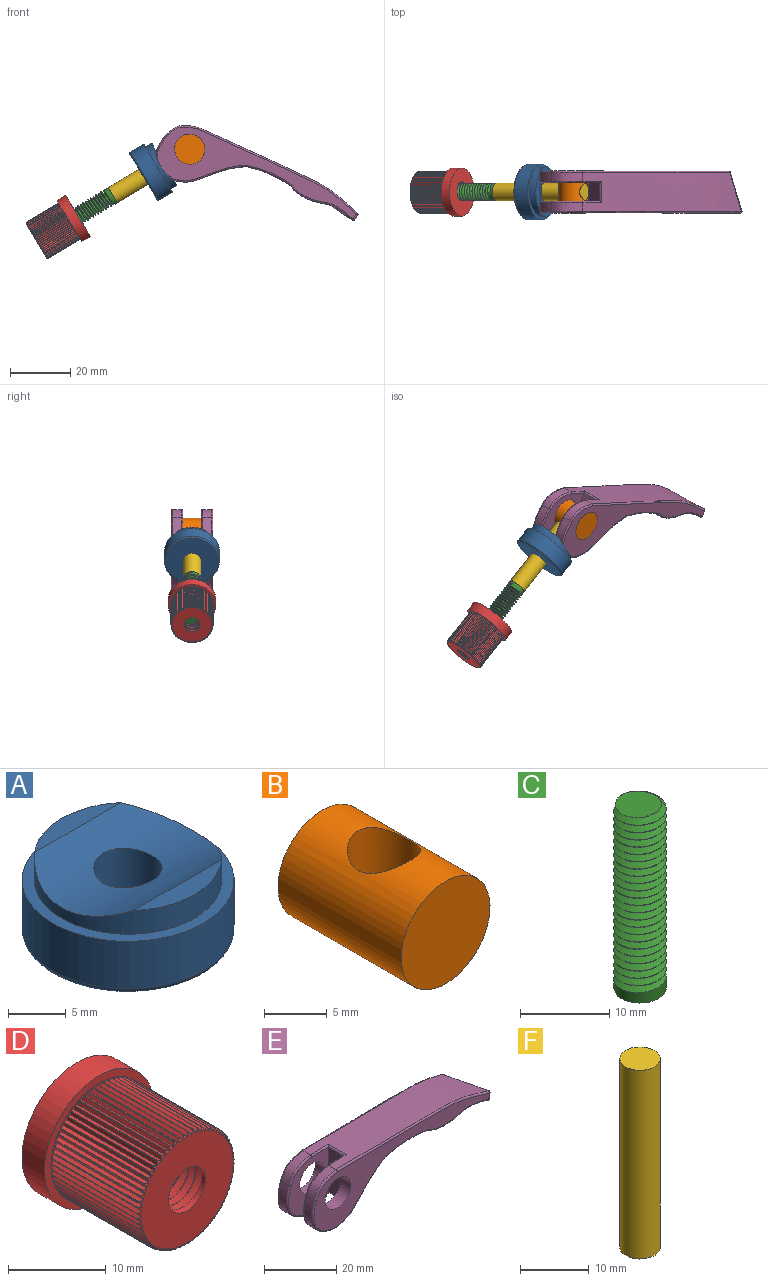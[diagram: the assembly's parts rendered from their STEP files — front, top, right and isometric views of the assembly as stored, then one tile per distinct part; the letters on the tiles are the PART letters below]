
ASSEMBLY  parts=6 mates=5
PART A: 9 faces, bbox 19.9x19.9x8.1 mm
  f0: plane 10.78x2.05mm, normal (0,0,1), area 15.1mm2, adj f5,f8
  f1: cylinder r=9.2mm len=18.4mm, axis (0,0,-1), area 291.9mm2, adj f2,f7
  f2: plane 18.4x18.4mm, normal (0,0,1), area 58.5mm2, adj f1,f5
  f3: plane 17.4x17.4mm, normal (0,0,-1), area 210.3mm2, adj f4,f7
  f4: cylinder r=2.96mm len=7mm, axis (0,0,-1), area 127mm2, adj f3,f8
  f5: cylinder r=8.12mm len=16.25mm, axis (0,0,-1), area 103.6mm2, adj f0,f2,f6,f8
  f6: plane 10.55x1.94mm, normal (0,0,1), area 14mm2, adj f5,f8
  f7: torus R=8.7mm, axis (0,0,1), area 44.5mm2, adj f1,f3
  f8: cylinder r=14.26mm len=16.25mm, axis (1,0,0), area 155.9mm2, adj f0,f4,f5,f6
PART B: 4 faces, bbox 10x13.9x10 mm
  f0: cylinder r=5mm len=13.9mm, axis (0,1,0), area 380.3mm2, adj f1,f2,f3
  f1: plane 10x10mm, normal (0,-1,0), area 78.5mm2, adj f0
  f2: plane 10x10mm, normal (0,1,0), area 78.5mm2, adj f0
  f3: cylinder r=2.93mm len=10mm, axis (0,0,-1), area 166.9mm2, adj f0
PART C: 30 faces, bbox 6.5x7.4x26.2 mm
  f0: cylinder r=2.95mm len=5.9mm, axis (0,0,-1), area 24.5mm2, adj f24,f26,f27,f28,f29
  f1: cylinder r=2.95mm len=0.13mm, axis (0,0,-1), area 0mm2, adj f2,f25,f28
  f2: cylinder r=2.95mm len=5.9mm, axis (0,0,-1), area 1.1mm2, adj f1,f3,f25,f27,f28
  f3: cylinder r=2.95mm len=5.9mm, axis (0,0,-1), area 1.2mm2, adj f2,f4,f27,f28
  f4: cylinder r=2.95mm len=5.9mm, axis (0,0,-1), area 1.2mm2, adj f3,f5,f27,f28
  f5: cylinder r=2.95mm len=5.9mm, axis (0,0,-1), area 1.2mm2, adj f4,f6,f27,f28
  f6: cylinder r=2.95mm len=5.9mm, axis (0,0,-1), area 1.2mm2, adj f5,f7,f27,f28
  f7: cylinder r=2.95mm len=5.9mm, axis (0,0,-1), area 1.2mm2, adj f6,f8,f27,f28
  f8: cylinder r=2.95mm len=5.9mm, axis (0,0,-1), area 1.2mm2, adj f7,f9,f27,f28
  f9: cylinder r=2.95mm len=5.9mm, axis (0,0,-1), area 1.2mm2, adj f8,f10,f27,f28
  f10: cylinder r=2.95mm len=5.9mm, axis (0,0,-1), area 1.2mm2, adj f9,f11,f27,f28
  f11: cylinder r=2.95mm len=5.9mm, axis (0,0,-1), area 1.2mm2, adj f10,f12,f27,f28
  f12: cylinder r=2.95mm len=5.9mm, axis (0,0,-1), area 1.2mm2, adj f11,f13,f27,f28
  f13: cylinder r=2.95mm len=5.9mm, axis (0,0,-1), area 1.2mm2, adj f12,f14,f27,f28
  f14: cylinder r=2.95mm len=5.9mm, axis (0,0,-1), area 1.2mm2, adj f13,f15,f27,f28
  f15: cylinder r=2.95mm len=5.9mm, axis (0,0,-1), area 1.2mm2, adj f14,f16,f27,f28
  f16: cylinder r=2.95mm len=5.9mm, axis (0,0,-1), area 1.2mm2, adj f15,f17,f27,f28
  f17: cylinder r=2.95mm len=5.9mm, axis (0,0,-1), area 1.2mm2, adj f16,f18,f27,f28
  f18: cylinder r=2.95mm len=5.9mm, axis (0,0,-1), area 1.2mm2, adj f17,f19,f27,f28
  f19: cylinder r=2.95mm len=5.9mm, axis (0,0,-1), area 1.2mm2, adj f18,f20,f27,f28
  f20: cylinder r=2.95mm len=5.9mm, axis (0,0,-1), area 1.2mm2, adj f19,f21,f27,f28
  f21: cylinder r=2.95mm len=5.9mm, axis (0,0,-1), area 1.2mm2, adj f20,f22,f27,f28
  f22: cylinder r=2.95mm len=5.9mm, axis (0,0,-1), area 1.2mm2, adj f21,f23,f27,f28
  f23: cylinder r=2.95mm len=5.9mm, axis (0,0,-1), area 1.2mm2, adj f22,f24,f27,f28
  f24: cylinder r=2.95mm len=5.9mm, axis (0,0,-1), area 1.2mm2, adj f0,f23,f27,f28
  f25: plane 5.73x5.71mm, normal (0,0,1), area 20.9mm2, adj f1,f2,f27,f28
  f26: plane 5.9x5.9mm, normal (0,0,-1), area 27.3mm2, adj f0
  f27: bspline ~24.81x6.84mm, area 362.6mm2, adj f0,f2,f3,f4,f5,f6,f7,f8
  f28: bspline ~24.31x6.84mm, area 352.4mm2, adj f0,f1,f2,f3,f4,f5,f6,f7
  f29: plane 0.94x0.81mm, normal (0,1,0), area 0.4mm2, adj f0,f27,f28
PART D: 280 faces, bbox 16.4x17.2x16.4 mm
  f0: cylinder r=7mm len=14mm, axis (0,1,0), area 36.4mm2, adj f2,f3,f4,f5,f6,f7,f8,f9
  f1: plane 13.34x13.34mm, normal (0,-1,0), area 117.5mm2, adj f2,f3,f4,f5,f6,f7,f8,f9
  f2: torus R=6.67mm, axis (0,-1,0), area 0.1mm2, adj f0,f1,f88,f278
  f3: torus R=6.67mm, axis (0,-1,0), area 0.1mm2, adj f0,f1,f275,f279
  f4: torus R=6.67mm, axis (0,-1,0), area 0.1mm2, adj f0,f1,f272,f274
  f5: torus R=6.67mm, axis (0,-1,0), area 0.1mm2, adj f0,f1,f269,f271
  f6: torus R=6.67mm, axis (0,-1,0), area 0.1mm2, adj f0,f1,f266,f268
  f7: torus R=6.67mm, axis (0,-1,0), area 0.1mm2, adj f0,f1,f263,f265
  f8: torus R=6.67mm, axis (0,-1,0), area 0.1mm2, adj f0,f1,f260,f262
  f9: torus R=6.67mm, axis (0,-1,0), area 0.1mm2, adj f0,f1,f257,f259
  f10: torus R=6.67mm, axis (0,-1,0), area 0.1mm2, adj f0,f1,f254,f256
  f11: torus R=6.67mm, axis (0,-1,0), area 0.1mm2, adj f0,f1,f251,f253
  f12: torus R=6.67mm, axis (0,-1,0), area 0.1mm2, adj f0,f1,f248,f250
  f13: torus R=6.67mm, axis (0,-1,0), area 0.1mm2, adj f0,f1,f245,f247
  f14: torus R=6.67mm, axis (0,-1,0), area 0.1mm2, adj f0,f1,f242,f244
  f15: torus R=6.67mm, axis (0,-1,0), area 0.1mm2, adj f0,f1,f239,f241
  f16: torus R=6.67mm, axis (0,-1,0), area 0.1mm2, adj f0,f1,f236,f238
  f17: torus R=6.67mm, axis (0,-1,0), area 0.1mm2, adj f0,f1,f233,f235
  f18: torus R=6.67mm, axis (0,-1,0), area 0.1mm2, adj f0,f1,f230,f232
  f19: torus R=6.67mm, axis (0,-1,0), area 0.1mm2, adj f0,f1,f227,f229
  f20: torus R=6.67mm, axis (0,-1,0), area 0.1mm2, adj f0,f1,f224,f226
  f21: torus R=6.67mm, axis (0,-1,0), area 0.1mm2, adj f0,f1,f221,f223
  f22: torus R=6.67mm, axis (0,-1,0), area 0.1mm2, adj f0,f1,f218,f220
  f23: torus R=6.67mm, axis (0,-1,0), area 0.1mm2, adj f0,f1,f215,f217
  f24: torus R=6.67mm, axis (0,-1,0), area 0.1mm2, adj f0,f1,f212,f214
  f25: torus R=6.67mm, axis (0,-1,0), area 0.1mm2, adj f0,f1,f209,f211
  f26: torus R=6.67mm, axis (0,-1,0), area 0.1mm2, adj f0,f1,f206,f208
  f27: torus R=6.67mm, axis (0,-1,0), area 0.1mm2, adj f0,f1,f203,f205
  f28: torus R=6.67mm, axis (0,-1,0), area 0.1mm2, adj f0,f1,f200,f202
  f29: torus R=6.67mm, axis (0,-1,0), area 0.1mm2, adj f0,f1,f197,f199
  f30: torus R=6.67mm, axis (0,-1,0), area 0.1mm2, adj f0,f1,f194,f196
  f31: torus R=6.67mm, axis (0,-1,0), area 0.1mm2, adj f0,f1,f191,f193
  f32: torus R=6.67mm, axis (0,-1,0), area 0.1mm2, adj f0,f1,f188,f190
  f33: torus R=6.67mm, axis (0,-1,0), area 0.1mm2, adj f0,f1,f185,f187
  f34: torus R=6.67mm, axis (0,-1,0), area 0.1mm2, adj f0,f1,f182,f184
  f35: torus R=6.67mm, axis (0,-1,0), area 0.1mm2, adj f0,f1,f179,f181
  f36: torus R=6.67mm, axis (0,-1,0), area 0.1mm2, adj f0,f1,f176,f178
  f37: torus R=6.67mm, axis (0,-1,0), area 0.1mm2, adj f0,f1,f173,f175
  f38: torus R=6.67mm, axis (0,-1,0), area 0.1mm2, adj f0,f1,f170,f172
  f39: torus R=6.67mm, axis (0,-1,0), area 0.1mm2, adj f0,f1,f167,f169
  f40: torus R=6.67mm, axis (0,-1,0), area 0.1mm2, adj f0,f1,f164,f166
  f41: torus R=6.67mm, axis (0,-1,0), area 0.1mm2, adj f0,f1,f161,f163
  f42: torus R=6.67mm, axis (0,-1,0), area 0.1mm2, adj f0,f1,f158,f160
  f43: torus R=6.67mm, axis (0,-1,0), area 0.1mm2, adj f0,f1,f155,f157
  f44: torus R=6.67mm, axis (0,-1,0), area 0.1mm2, adj f0,f1,f152,f154
  f45: torus R=6.67mm, axis (0,-1,0), area 0.1mm2, adj f0,f1,f149,f151
  f46: torus R=6.67mm, axis (0,-1,0), area 0.1mm2, adj f0,f1,f146,f148
  f47: torus R=6.67mm, axis (0,-1,0), area 0.1mm2, adj f0,f1,f143,f145
  f48: torus R=6.67mm, axis (0,-1,0), area 0.1mm2, adj f0,f1,f140,f142
  f49: torus R=6.67mm, axis (0,-1,0), area 0.1mm2, adj f0,f1,f137,f139
  f50: torus R=6.67mm, axis (0,-1,0), area 0.1mm2, adj f0,f1,f134,f136
  f51: torus R=6.67mm, axis (0,-1,0), area 0.1mm2, adj f0,f1,f131,f133
  f52: torus R=6.67mm, axis (0,-1,0), area 0.1mm2, adj f0,f1,f128,f130
  f53: torus R=6.67mm, axis (0,-1,0), area 0.1mm2, adj f0,f1,f125,f127
  f54: torus R=6.67mm, axis (0,-1,0), area 0.1mm2, adj f0,f1,f122,f124
  f55: torus R=6.67mm, axis (0,-1,0), area 0.1mm2, adj f0,f1,f119,f121
  f56: torus R=6.67mm, axis (0,-1,0), area 0.1mm2, adj f0,f1,f116,f118
  f57: torus R=6.67mm, axis (0,-1,0), area 0.1mm2, adj f0,f1,f113,f115
  f58: torus R=6.67mm, axis (0,-1,0), area 0.1mm2, adj f0,f1,f110,f112
  f59: torus R=6.67mm, axis (0,-1,0), area 0.1mm2, adj f0,f1,f107,f109
  f60: torus R=6.67mm, axis (0,-1,0), area 0.1mm2, adj f0,f1,f104,f106
  f61: torus R=6.67mm, axis (0,-1,0), area 0.1mm2, adj f0,f1,f101,f103
  f62: torus R=6.67mm, axis (0,-1,0), area 0.1mm2, adj f0,f1,f98,f100
  f63: torus R=6.67mm, axis (0,-1,0), area 0.1mm2, adj f0,f1,f95,f97
  f64: torus R=6.67mm, axis (0,-1,0), area 0.1mm2, adj f0,f1,f92,f94
  f65: torus R=6.67mm, axis (0,-1,0), area 0.1mm2, adj f0,f1,f89,f91
  f66: cylinder r=7.95mm len=15.9mm, axis (0,1,0), area 162.3mm2, adj f67,f68
  f67: plane 15.9x15.9mm, normal (0,-1,0), area 44.6mm2, adj f0,f66
  f68: plane 16.45x16.45mm, normal (0,1,0), area 169.7mm2, adj f66,f84,f85,f86
  f69: cylinder r=2.67mm len=5.33mm, axis (0,1,0), area 8.9mm2, adj f1,f70,f85,f86,f87
  f70: cylinder r=2.67mm len=5.33mm, axis (0,1,0), area 1.6mm2, adj f69,f71,f85,f86
  f71: cylinder r=2.67mm len=5.33mm, axis (0,1,0), area 1.6mm2, adj f70,f72,f85,f86
  f72: cylinder r=2.67mm len=5.33mm, axis (0,1,0), area 1.6mm2, adj f71,f73,f85,f86
  f73: cylinder r=2.67mm len=5.33mm, axis (0,1,0), area 1.6mm2, adj f72,f74,f85,f86
  f74: cylinder r=2.67mm len=5.33mm, axis (0,1,0), area 1.6mm2, adj f73,f75,f85,f86
  f75: cylinder r=2.67mm len=5.33mm, axis (0,1,0), area 1.6mm2, adj f74,f76,f85,f86
  f76: cylinder r=2.67mm len=5.33mm, axis (0,1,0), area 1.6mm2, adj f75,f77,f85,f86
  f77: cylinder r=2.67mm len=5.33mm, axis (0,1,0), area 1.6mm2, adj f76,f78,f85,f86
  f78: cylinder r=2.67mm len=5.33mm, axis (0,1,0), area 1.6mm2, adj f77,f79,f85,f86
  f79: cylinder r=2.67mm len=5.33mm, axis (0,1,0), area 1.6mm2, adj f78,f80,f85,f86
  f80: cylinder r=2.67mm len=5.33mm, axis (0,1,0), area 1.6mm2, adj f79,f81,f85,f86
  f81: cylinder r=2.67mm len=5.33mm, axis (0,1,0), area 1.6mm2, adj f80,f82,f85,f86
  f82: cylinder r=2.67mm len=5.33mm, axis (0,1,0), area 1.6mm2, adj f81,f83,f85,f86
  f83: cylinder r=2.67mm len=5.33mm, axis (0,1,0), area 1.6mm2, adj f82,f84,f85,f86
  f84: cylinder r=2.67mm len=5.33mm, axis (0,1,0), area 1.5mm2, adj f68,f83,f85,f86
  f85: bspline ~16.47x7.96mm, area 271.9mm2, adj f68,f69,f70,f71,f72,f73,f74,f75
  f86: bspline ~16.15x7.96mm, area 267.8mm2, adj f68,f69,f70,f71,f72,f73,f74,f75
  f87: plane 0.9x0.78mm, normal (0,0,1), area 0.4mm2, adj f69,f85,f86
  f88: plane 12.7x0.36mm, normal (-0.78,0,0.63), area 5.8mm2, adj f0,f1,f2,f89,f90
  f89: plane 12.7x0.35mm, normal (0.64,0,0.77), area 5.8mm2, adj f0,f1,f65,f88,f90
  f90: plane 0.64x0.36mm, normal (0,-1,0), area 0.1mm2, adj f0,f88,f89
  f91: plane 12.7x0.38mm, normal (-0.84,0,0.55), area 5.8mm2, adj f0,f1,f65,f92,f93
  f92: plane 12.7x0.38mm, normal (0.56,0,0.83), area 5.8mm2, adj f0,f1,f64,f91,f93
  f93: plane 0.63x0.38mm, normal (0,-1,0), area 0.1mm2, adj f0,f91,f92
  f94: plane 12.7x0.41mm, normal (-0.89,0,0.46), area 5.8mm2, adj f0,f1,f64,f95,f96
  f95: plane 12.7x0.4mm, normal (0.48,0,0.88), area 5.8mm2, adj f0,f1,f63,f94,f96
  f96: plane 0.62x0.41mm, normal (0,-1,0), area 0.1mm2, adj f0,f94,f95
  f97: plane 12.7x0.43mm, normal (-0.93,0,0.38), area 5.8mm2, adj f0,f1,f63,f98,f99
  f98: plane 12.7x0.42mm, normal (0.39,0,0.92), area 5.8mm2, adj f0,f1,f62,f97,f99
  f99: plane 0.59x0.43mm, normal (0,-1,0), area 0.1mm2, adj f0,f97,f98
  f100: plane 12.7x0.44mm, normal (-0.96,0,0.28), area 5.8mm2, adj f0,f1,f62,f101,f102
  f101: plane 12.7x0.44mm, normal (0.3,0,0.95), area 5.8mm2, adj f0,f1,f61,f100,f102
  f102: plane 0.57x0.44mm, normal (0,-1,0), area 0.1mm2, adj f0,f100,f101
  f103: plane 12.7x0.45mm, normal (-0.98,0,0.19), area 5.8mm2, adj f0,f1,f61,f104,f105
  f104: plane 12.7x0.45mm, normal (0.2,0,0.98), area 5.8mm2, adj f0,f1,f60,f103,f105
  f105: plane 0.54x0.45mm, normal (0,-1,0), area 0.1mm2, adj f0,f103,f104
  f106: plane 12.7x0.46mm, normal (-1,0,0.09), area 5.8mm2, adj f0,f1,f60,f107,f108
  f107: plane 12.7x0.46mm, normal (0.11,0,0.99), area 5.8mm2, adj f0,f1,f59,f106,f108
  f108: plane 0.5x0.46mm, normal (0,-1,0), area 0.1mm2, adj f0,f106,f107
  f109: plane 12.7x0.46mm, normal (-1,0,-0.01), area 5.8mm2, adj f0,f1,f59,f110,f111
  f110: plane 12.7x0.46mm, normal (0.01,0,1), area 5.8mm2, adj f0,f1,f58,f109,f111
  f111: plane 0.46x0.46mm, normal (0,-1,0), area 0.1mm2, adj f0,f109,f110
  f112: plane 12.7x0.46mm, normal (-0.99,0,-0.11), area 5.8mm2, adj f0,f1,f58,f113,f114
  f113: plane 12.7x0.46mm, normal (-0.09,0,1), area 5.8mm2, adj f0,f1,f57,f112,f114
  f114: plane 0.5x0.46mm, normal (0,-1,0), area 0.1mm2, adj f0,f112,f113
  f115: plane 12.7x0.45mm, normal (-0.98,0,-0.2), area 5.8mm2, adj f0,f1,f57,f116,f117
  f116: plane 12.7x0.45mm, normal (-0.19,0,0.98), area 5.8mm2, adj f0,f1,f56,f115,f117
  f117: plane 0.54x0.45mm, normal (0,-1,0), area 0.1mm2, adj f0,f115,f116
  f118: plane 12.7x0.44mm, normal (-0.95,0,-0.3), area 5.8mm2, adj f0,f1,f56,f119,f120
  f119: plane 12.7x0.44mm, normal (-0.28,0,0.96), area 5.8mm2, adj f0,f1,f55,f118,f120
  f120: plane 0.57x0.44mm, normal (0,-1,0), area 0.1mm2, adj f0,f118,f119
  f121: plane 12.7x0.42mm, normal (-0.92,0,-0.39), area 5.8mm2, adj f0,f1,f55,f122,f123
  f122: plane 12.7x0.43mm, normal (-0.38,0,0.93), area 5.8mm2, adj f0,f1,f54,f121,f123
  f123: plane 0.59x0.43mm, normal (0,-1,0), area 0.1mm2, adj f0,f121,f122
  f124: plane 12.7x0.4mm, normal (-0.88,0,-0.48), area 5.8mm2, adj f0,f1,f54,f125,f126
  f125: plane 12.7x0.41mm, normal (-0.46,0,0.89), area 5.8mm2, adj f0,f1,f53,f124,f126
  f126: plane 0.62x0.41mm, normal (0,-1,0), area 0.1mm2, adj f0,f124,f125
  f127: plane 12.7x0.38mm, normal (-0.83,0,-0.56), area 5.8mm2, adj f0,f1,f53,f128,f129
  f128: plane 12.7x0.38mm, normal (-0.55,0,0.84), area 5.8mm2, adj f0,f1,f52,f127,f129
  f129: plane 0.63x0.38mm, normal (0,-1,0), area 0.1mm2, adj f0,f127,f128
  f130: plane 12.7x0.35mm, normal (-0.77,0,-0.64), area 5.8mm2, adj f0,f1,f52,f131,f132
  f131: plane 12.7x0.36mm, normal (-0.63,0,0.78), area 5.8mm2, adj f0,f1,f51,f130,f132
  f132: plane 0.64x0.36mm, normal (0,-1,0), area 0.1mm2, adj f0,f130,f131
  f133: plane 12.7x0.33mm, normal (-0.7,0,-0.71), area 5.8mm2, adj f0,f1,f51,f134,f135
  f134: plane 12.7x0.33mm, normal (-0.7,0,0.71), area 5.8mm2, adj f0,f1,f50,f133,f135
  f135: plane 0.64x0.33mm, normal (0,-1,0), area 0.1mm2, adj f0,f133,f134
  f136: plane 12.7x0.36mm, normal (-0.63,0,-0.78), area 5.8mm2, adj f0,f1,f50,f137,f138
  f137: plane 12.7x0.35mm, normal (-0.77,0,0.64), area 5.8mm2, adj f0,f1,f49,f136,f138
  f138: plane 0.64x0.36mm, normal (0,-1,0), area 0.1mm2, adj f0,f136,f137
  f139: plane 12.7x0.38mm, normal (-0.55,0,-0.84), area 5.8mm2, adj f0,f1,f49,f140,f141
  f140: plane 12.7x0.38mm, normal (-0.83,0,0.56), area 5.8mm2, adj f0,f1,f48,f139,f141
  f141: plane 0.63x0.38mm, normal (0,-1,0), area 0.1mm2, adj f0,f139,f140
  f142: plane 12.7x0.41mm, normal (-0.46,0,-0.89), area 5.8mm2, adj f0,f1,f48,f143,f144
  f143: plane 12.7x0.4mm, normal (-0.88,0,0.48), area 5.8mm2, adj f0,f1,f47,f142,f144
  f144: plane 0.62x0.41mm, normal (0,-1,0), area 0.1mm2, adj f0,f142,f143
  f145: plane 12.7x0.43mm, normal (-0.38,0,-0.93), area 5.8mm2, adj f0,f1,f47,f146,f147
  f146: plane 12.7x0.42mm, normal (-0.92,0,0.39), area 5.8mm2, adj f0,f1,f46,f145,f147
  f147: plane 0.59x0.43mm, normal (0,-1,0), area 0.1mm2, adj f0,f145,f146
  f148: plane 12.7x0.44mm, normal (-0.28,0,-0.96), area 5.8mm2, adj f0,f1,f46,f149,f150
  f149: plane 12.7x0.44mm, normal (-0.95,0,0.3), area 5.8mm2, adj f0,f1,f45,f148,f150
  f150: plane 0.57x0.44mm, normal (0,-1,0), area 0.1mm2, adj f0,f148,f149
  f151: plane 12.7x0.45mm, normal (-0.19,0,-0.98), area 5.8mm2, adj f0,f1,f45,f152,f153
  f152: plane 12.7x0.45mm, normal (-0.98,0,0.2), area 5.8mm2, adj f0,f1,f44,f151,f153
  f153: plane 0.54x0.45mm, normal (0,-1,0), area 0.1mm2, adj f0,f151,f152
  f154: plane 12.7x0.46mm, normal (-0.09,0,-1), area 5.8mm2, adj f0,f1,f44,f155,f156
  f155: plane 12.7x0.46mm, normal (-0.99,0,0.11), area 5.8mm2, adj f0,f1,f43,f154,f156
  f156: plane 0.5x0.46mm, normal (0,-1,0), area 0.1mm2, adj f0,f154,f155
  f157: plane 12.7x0.46mm, normal (0.01,0,-1), area 5.8mm2, adj f0,f1,f43,f158,f159
  f158: plane 12.7x0.46mm, normal (-1,0,0.01), area 5.8mm2, adj f0,f1,f42,f157,f159
  f159: plane 0.46x0.46mm, normal (0,-1,0), area 0.1mm2, adj f0,f157,f158
  f160: plane 12.7x0.46mm, normal (0.11,0,-0.99), area 5.8mm2, adj f0,f1,f42,f161,f162
  f161: plane 12.7x0.46mm, normal (-1,0,-0.09), area 5.8mm2, adj f0,f1,f41,f160,f162
  f162: plane 0.5x0.46mm, normal (0,-1,0), area 0.1mm2, adj f0,f160,f161
  f163: plane 12.7x0.45mm, normal (0.2,0,-0.98), area 5.8mm2, adj f0,f1,f41,f164,f165
  f164: plane 12.7x0.45mm, normal (-0.98,0,-0.19), area 5.8mm2, adj f0,f1,f40,f163,f165
  f165: plane 0.54x0.45mm, normal (0,-1,0), area 0.1mm2, adj f0,f163,f164
  f166: plane 12.7x0.44mm, normal (0.3,0,-0.95), area 5.8mm2, adj f0,f1,f40,f167,f168
  f167: plane 12.7x0.44mm, normal (-0.96,0,-0.28), area 5.8mm2, adj f0,f1,f39,f166,f168
  f168: plane 0.57x0.44mm, normal (0,-1,0), area 0.1mm2, adj f0,f166,f167
  f169: plane 12.7x0.42mm, normal (0.39,0,-0.92), area 5.8mm2, adj f0,f1,f39,f170,f171
  f170: plane 12.7x0.43mm, normal (-0.93,0,-0.38), area 5.8mm2, adj f0,f1,f38,f169,f171
  f171: plane 0.59x0.43mm, normal (0,-1,0), area 0.1mm2, adj f0,f169,f170
  f172: plane 12.7x0.4mm, normal (0.48,0,-0.88), area 5.8mm2, adj f0,f1,f38,f173,f174
  f173: plane 12.7x0.41mm, normal (-0.89,0,-0.46), area 5.8mm2, adj f0,f1,f37,f172,f174
  f174: plane 0.62x0.41mm, normal (0,-1,0), area 0.1mm2, adj f0,f172,f173
  f175: plane 12.7x0.38mm, normal (0.56,0,-0.83), area 5.8mm2, adj f0,f1,f37,f176,f177
  f176: plane 12.7x0.38mm, normal (-0.84,0,-0.55), area 5.8mm2, adj f0,f1,f36,f175,f177
  f177: plane 0.63x0.38mm, normal (0,-1,0), area 0.1mm2, adj f0,f175,f176
  f178: plane 12.7x0.35mm, normal (0.64,0,-0.77), area 5.8mm2, adj f0,f1,f36,f179,f180
  f179: plane 12.7x0.36mm, normal (-0.78,0,-0.63), area 5.8mm2, adj f0,f1,f35,f178,f180
  f180: plane 0.64x0.36mm, normal (0,-1,0), area 0.1mm2, adj f0,f178,f179
  f181: plane 12.7x0.33mm, normal (0.71,0,-0.7), area 5.8mm2, adj f0,f1,f35,f182,f183
  f182: plane 12.7x0.33mm, normal (-0.71,0,-0.7), area 5.8mm2, adj f0,f1,f34,f181,f183
  f183: plane 0.64x0.33mm, normal (0,-1,0), area 0.1mm2, adj f0,f181,f182
  f184: plane 12.7x0.36mm, normal (0.78,0,-0.63), area 5.8mm2, adj f0,f1,f34,f185,f186
  f185: plane 12.7x0.35mm, normal (-0.64,0,-0.77), area 5.8mm2, adj f0,f1,f33,f184,f186
  f186: plane 0.64x0.36mm, normal (0,-1,0), area 0.1mm2, adj f0,f184,f185
  f187: plane 12.7x0.38mm, normal (0.84,0,-0.55), area 5.8mm2, adj f0,f1,f33,f188,f189
  f188: plane 12.7x0.38mm, normal (-0.56,0,-0.83), area 5.8mm2, adj f0,f1,f32,f187,f189
  f189: plane 0.63x0.38mm, normal (0,-1,0), area 0.1mm2, adj f0,f187,f188
  f190: plane 12.7x0.41mm, normal (0.89,0,-0.46), area 5.8mm2, adj f0,f1,f32,f191,f192
  f191: plane 12.7x0.4mm, normal (-0.48,0,-0.88), area 5.8mm2, adj f0,f1,f31,f190,f192
  f192: plane 0.62x0.41mm, normal (0,-1,0), area 0.1mm2, adj f0,f190,f191
  f193: plane 12.7x0.43mm, normal (0.93,0,-0.38), area 5.8mm2, adj f0,f1,f31,f194,f195
  f194: plane 12.7x0.42mm, normal (-0.39,0,-0.92), area 5.8mm2, adj f0,f1,f30,f193,f195
  f195: plane 0.59x0.43mm, normal (0,-1,0), area 0.1mm2, adj f0,f193,f194
  f196: plane 12.7x0.44mm, normal (0.96,0,-0.28), area 5.8mm2, adj f0,f1,f30,f197,f198
  f197: plane 12.7x0.44mm, normal (-0.3,0,-0.95), area 5.8mm2, adj f0,f1,f29,f196,f198
  f198: plane 0.57x0.44mm, normal (0,-1,0), area 0.1mm2, adj f0,f196,f197
  f199: plane 12.7x0.45mm, normal (0.98,0,-0.19), area 5.8mm2, adj f0,f1,f29,f200,f201
  f200: plane 12.7x0.45mm, normal (-0.2,0,-0.98), area 5.8mm2, adj f0,f1,f28,f199,f201
  f201: plane 0.54x0.45mm, normal (0,-1,0), area 0.1mm2, adj f0,f199,f200
  f202: plane 12.7x0.46mm, normal (1,0,-0.09), area 5.8mm2, adj f0,f1,f28,f203,f204
  f203: plane 12.7x0.46mm, normal (-0.11,0,-0.99), area 5.8mm2, adj f0,f1,f27,f202,f204
  f204: plane 0.5x0.46mm, normal (0,-1,0), area 0.1mm2, adj f0,f202,f203
  f205: plane 12.7x0.46mm, normal (1,0,0.01), area 5.8mm2, adj f0,f1,f27,f206,f207
  f206: plane 12.7x0.46mm, normal (-0.01,0,-1), area 5.8mm2, adj f0,f1,f26,f205,f207
  f207: plane 0.46x0.46mm, normal (0,-1,0), area 0.1mm2, adj f0,f205,f206
  f208: plane 12.7x0.46mm, normal (0.99,0,0.11), area 5.8mm2, adj f0,f1,f26,f209,f210
  f209: plane 12.7x0.46mm, normal (0.09,0,-1), area 5.8mm2, adj f0,f1,f25,f208,f210
  f210: plane 0.5x0.46mm, normal (0,-1,0), area 0.1mm2, adj f0,f208,f209
  f211: plane 12.7x0.45mm, normal (0.98,0,0.2), area 5.8mm2, adj f0,f1,f25,f212,f213
  f212: plane 12.7x0.45mm, normal (0.19,0,-0.98), area 5.8mm2, adj f0,f1,f24,f211,f213
  f213: plane 0.54x0.45mm, normal (0,-1,0), area 0.1mm2, adj f0,f211,f212
  f214: plane 12.7x0.44mm, normal (0.95,0,0.3), area 5.8mm2, adj f0,f1,f24,f215,f216
  f215: plane 12.7x0.44mm, normal (0.28,0,-0.96), area 5.8mm2, adj f0,f1,f23,f214,f216
  f216: plane 0.57x0.44mm, normal (0,-1,0), area 0.1mm2, adj f0,f214,f215
  f217: plane 12.7x0.42mm, normal (0.92,0,0.39), area 5.8mm2, adj f0,f1,f23,f218,f219
  f218: plane 12.7x0.43mm, normal (0.38,0,-0.93), area 5.8mm2, adj f0,f1,f22,f217,f219
  f219: plane 0.59x0.43mm, normal (0,-1,0), area 0.1mm2, adj f0,f217,f218
  f220: plane 12.7x0.4mm, normal (0.88,0,0.48), area 5.8mm2, adj f0,f1,f22,f221,f222
  f221: plane 12.7x0.41mm, normal (0.46,0,-0.89), area 5.8mm2, adj f0,f1,f21,f220,f222
  f222: plane 0.62x0.41mm, normal (0,-1,0), area 0.1mm2, adj f0,f220,f221
  f223: plane 12.7x0.38mm, normal (0.83,0,0.56), area 5.8mm2, adj f0,f1,f21,f224,f225
  f224: plane 12.7x0.38mm, normal (0.55,0,-0.84), area 5.8mm2, adj f0,f1,f20,f223,f225
  f225: plane 0.63x0.38mm, normal (0,-1,0), area 0.1mm2, adj f0,f223,f224
  f226: plane 12.7x0.35mm, normal (0.77,0,0.64), area 5.8mm2, adj f0,f1,f20,f227,f228
  f227: plane 12.7x0.36mm, normal (0.63,0,-0.78), area 5.8mm2, adj f0,f1,f19,f226,f228
  f228: plane 0.64x0.36mm, normal (0,-1,0), area 0.1mm2, adj f0,f226,f227
  f229: plane 12.7x0.33mm, normal (0.7,0,0.71), area 5.8mm2, adj f0,f1,f19,f230,f231
  f230: plane 12.7x0.33mm, normal (0.7,0,-0.71), area 5.8mm2, adj f0,f1,f18,f229,f231
  f231: plane 0.64x0.33mm, normal (0,-1,0), area 0.1mm2, adj f0,f229,f230
  f232: plane 12.7x0.36mm, normal (0.63,0,0.78), area 5.8mm2, adj f0,f1,f18,f233,f234
  f233: plane 12.7x0.35mm, normal (0.77,0,-0.64), area 5.8mm2, adj f0,f1,f17,f232,f234
  f234: plane 0.64x0.36mm, normal (0,-1,0), area 0.1mm2, adj f0,f232,f233
  f235: plane 12.7x0.38mm, normal (0.55,0,0.84), area 5.8mm2, adj f0,f1,f17,f236,f237
  f236: plane 12.7x0.38mm, normal (0.83,0,-0.56), area 5.8mm2, adj f0,f1,f16,f235,f237
  f237: plane 0.63x0.38mm, normal (0,-1,0), area 0.1mm2, adj f0,f235,f236
  f238: plane 12.7x0.41mm, normal (0.46,0,0.89), area 5.8mm2, adj f0,f1,f16,f239,f240
  f239: plane 12.7x0.4mm, normal (0.88,0,-0.48), area 5.8mm2, adj f0,f1,f15,f238,f240
  f240: plane 0.62x0.41mm, normal (0,-1,0), area 0.1mm2, adj f0,f238,f239
  f241: plane 12.7x0.43mm, normal (0.38,0,0.93), area 5.8mm2, adj f0,f1,f15,f242,f243
  f242: plane 12.7x0.42mm, normal (0.92,0,-0.39), area 5.8mm2, adj f0,f1,f14,f241,f243
  f243: plane 0.59x0.43mm, normal (0,-1,0), area 0.1mm2, adj f0,f241,f242
  f244: plane 12.7x0.44mm, normal (0.28,0,0.96), area 5.8mm2, adj f0,f1,f14,f245,f246
  f245: plane 12.7x0.44mm, normal (0.95,0,-0.3), area 5.8mm2, adj f0,f1,f13,f244,f246
  f246: plane 0.57x0.44mm, normal (0,-1,0), area 0.1mm2, adj f0,f244,f245
  f247: plane 12.7x0.45mm, normal (0.19,0,0.98), area 5.8mm2, adj f0,f1,f13,f248,f249
  f248: plane 12.7x0.45mm, normal (0.98,0,-0.2), area 5.8mm2, adj f0,f1,f12,f247,f249
  f249: plane 0.54x0.45mm, normal (0,-1,0), area 0.1mm2, adj f0,f247,f248
  f250: plane 12.7x0.46mm, normal (0.09,0,1), area 5.8mm2, adj f0,f1,f12,f251,f252
  f251: plane 12.7x0.46mm, normal (0.99,0,-0.11), area 5.8mm2, adj f0,f1,f11,f250,f252
  f252: plane 0.5x0.46mm, normal (0,-1,0), area 0.1mm2, adj f0,f250,f251
  f253: plane 12.7x0.46mm, normal (-0.01,0,1), area 5.8mm2, adj f0,f1,f11,f254,f255
  f254: plane 12.7x0.46mm, normal (1,0,-0.01), area 5.8mm2, adj f0,f1,f10,f253,f255
  f255: plane 0.46x0.46mm, normal (0,-1,0), area 0.1mm2, adj f0,f253,f254
  f256: plane 12.7x0.46mm, normal (-0.11,0,0.99), area 5.8mm2, adj f0,f1,f10,f257,f258
  f257: plane 12.7x0.46mm, normal (1,0,0.09), area 5.8mm2, adj f0,f1,f9,f256,f258
  f258: plane 0.5x0.46mm, normal (0,-1,0), area 0.1mm2, adj f0,f256,f257
  f259: plane 12.7x0.45mm, normal (-0.2,0,0.98), area 5.8mm2, adj f0,f1,f9,f260,f261
  f260: plane 12.7x0.45mm, normal (0.98,0,0.19), area 5.8mm2, adj f0,f1,f8,f259,f261
  f261: plane 0.54x0.45mm, normal (0,-1,0), area 0.1mm2, adj f0,f259,f260
  f262: plane 12.7x0.44mm, normal (-0.3,0,0.95), area 5.8mm2, adj f0,f1,f8,f263,f264
  f263: plane 12.7x0.44mm, normal (0.96,0,0.28), area 5.8mm2, adj f0,f1,f7,f262,f264
  f264: plane 0.57x0.44mm, normal (0,-1,0), area 0.1mm2, adj f0,f262,f263
  f265: plane 12.7x0.42mm, normal (-0.39,0,0.92), area 5.8mm2, adj f0,f1,f7,f266,f267
  f266: plane 12.7x0.43mm, normal (0.93,0,0.38), area 5.8mm2, adj f0,f1,f6,f265,f267
  f267: plane 0.59x0.43mm, normal (0,-1,0), area 0.1mm2, adj f0,f265,f266
  f268: plane 12.7x0.4mm, normal (-0.48,0,0.88), area 5.8mm2, adj f0,f1,f6,f269,f270
  f269: plane 12.7x0.41mm, normal (0.89,0,0.46), area 5.8mm2, adj f0,f1,f5,f268,f270
  f270: plane 0.62x0.41mm, normal (0,-1,0), area 0.1mm2, adj f0,f268,f269
  f271: plane 12.7x0.38mm, normal (-0.56,0,0.83), area 5.8mm2, adj f0,f1,f5,f272,f273
  f272: plane 12.7x0.38mm, normal (0.84,0,0.55), area 5.8mm2, adj f0,f1,f4,f271,f273
  f273: plane 0.63x0.38mm, normal (0,-1,0), area 0.1mm2, adj f0,f271,f272
  f274: plane 12.7x0.35mm, normal (-0.64,0,0.77), area 5.8mm2, adj f0,f1,f4,f275,f276
  f275: plane 12.7x0.36mm, normal (0.78,0,0.63), area 5.8mm2, adj f0,f1,f3,f274,f276
  f276: plane 0.64x0.36mm, normal (0,-1,0), area 0.1mm2, adj f0,f274,f275
  f277: plane 0.64x0.33mm, normal (0,-1,0), area 0.1mm2, adj f0,f278,f279
  f278: plane 12.7x0.33mm, normal (0.71,0,0.7), area 5.8mm2, adj f0,f1,f2,f277,f279
  f279: plane 12.7x0.33mm, normal (-0.71,0,0.7), area 5.8mm2, adj f0,f1,f3,f277,f278
PART E: 46 faces, bbox 76.4x18.4x20.2 mm
  f0: extruded ~59.61x12.9mm, area 692.2mm2, adj f1,f5,f23,f24,f25,f31,f39,f40
  f1: extruded ~8.51x6.04mm, area 32.4mm2, adj f0,f2,f22,f35
  f2: extruded ~13.33x10.09mm, area 58.6mm2, adj f1,f3,f20,f30
  f3: extruded ~19.17x14.31mm, area 258mm2, adj f2,f6,f7,f16,f17,f18,f27,f34
  f4: cylinder r=5mm len=10mm, axis (0,1,0), area 123.3mm2, adj f10,f14
  f5: extruded ~8.51x6.04mm, area 32.4mm2, adj f0,f6,f21,f28
  f6: extruded ~13.33x10.09mm, area 58.6mm2, adj f3,f5,f19,f26
  f7: extruded ~16.25x12.9mm, area 211.7mm2, adj f3,f8,f29,f38
  f8: extruded ~23.01x12.9mm, area 270.2mm2, adj f7,f33,f41,f42
  f9: cylinder r=5mm len=10mm, axis (0,1,0), area 123.3mm2, adj f11,f15
  f10: plane 68.5x18.84mm, normal (0,-1,0), area 431.2mm2, adj f4,f30,f34,f35,f38,f39,f42,f45
  f11: plane 63.53x18.84mm, normal (0,1,0), area 421mm2, adj f9,f26,f27,f28,f29,f31,f32,f33
  f12: plane 12.91x5.35mm, normal (0.91,0.37,-0.16), area 27.4mm2, adj f32,f40,f41,f45
  f13: plane 14.85x6.05mm, normal (-1,0,0), area 89.9mm2, adj f14,f15,f16,f23,f24,f25
  f14: plane 18.47x15.57mm, normal (0,1,0), area 164.5mm2, adj f4,f13,f16,f18,f20,f22,f24
  f15: plane 18.47x15.57mm, normal (0,-1,0), area 164.5mm2, adj f9,f13,f16,f17,f19,f21,f23
  f16: cylinder r=0.5mm len=7.05mm, axis (0,1,0), area 7.5mm2, adj f3,f13,f14,f15,f17,f18
  f17: bspline ~7.74x4.78mm, area 5.8mm2, adj f3,f15,f16,f19
  f18: bspline ~7.74x4.78mm, area 5.8mm2, adj f3,f14,f16,f20
  f19: bspline ~13.86x10.16mm, area 15.4mm2, adj f6,f15,f17,f21
  f20: bspline ~13.86x10.38mm, area 15.4mm2, adj f2,f14,f18,f22
  f21: bspline ~8.85x6.46mm, area 8.5mm2, adj f5,f15,f19,f23
  f22: bspline ~8.85x6.46mm, area 8.5mm2, adj f1,f14,f20,f24
  f23: bspline ~34.65x1.04mm, area 5.2mm2, adj f0,f13,f15,f21,f25
  f24: bspline ~34.65x1.04mm, area 5.2mm2, adj f0,f13,f14,f22,f25
  f25: cylinder r=0.5mm len=7.05mm, axis (0,1,0), area 5.1mm2, adj f0,f13,f23,f24
  f26: bspline ~13.86x10.16mm, area 15.4mm2, adj f6,f11,f27,f28
  f27: bspline ~21.66x15.73mm, area 19mm2, adj f3,f11,f26,f29
  f28: bspline ~8.85x6.46mm, area 8.5mm2, adj f5,f11,f26,f31
  f29: bspline ~20.86x2.21mm, area 13mm2, adj f7,f11,f27,f33
  f30: bspline ~13.86x10.38mm, area 15.4mm2, adj f2,f10,f34,f35
  f31: bspline ~71.47x2.96mm, area 43mm2, adj f0,f11,f28,f36
  f32: cylinder r=0.5mm len=2.23mm, axis (-0.17,0,-0.98), area 1.3mm2, adj f11,f12,f36,f37
  f33: bspline ~19.29x1.96mm, area 14.5mm2, adj f8,f11,f29,f37
  f34: bspline ~21.3x15.4mm, area 19mm2, adj f3,f10,f30,f38
  f35: bspline ~8.85x6.46mm, area 8.5mm2, adj f1,f10,f30,f39
  f36: sphere r=0.5mm, area 0.2mm2, adj f31,f32,f40
  f37: sphere r=0.5mm, area 0.4mm2, adj f32,f33,f41
  f38: bspline ~20.86x2.21mm, area 13mm2, adj f7,f10,f34,f42
  f39: bspline ~65.24x4.26mm, area 47.1mm2, adj f0,f10,f35,f43
  f40: bspline ~18.41x7.43mm, area 10.2mm2, adj f0,f12,f36,f43
  f41: bspline ~17.72x7.34mm, area 11.3mm2, adj f8,f12,f37,f44
  f42: bspline ~24.44x2.28mm, area 18.5mm2, adj f8,f10,f38,f44
  f43: sphere r=0.5mm, area 0.5mm2, adj f39,f40,f45
  f44: sphere r=0.5mm, area 0.6mm2, adj f41,f42,f45
  f45: cylinder r=0.5mm len=1.99mm, axis (0.17,0,0.98), area 1.9mm2, adj f10,f12,f43,f44
PART F: 3 faces, bbox 5.9x5.9x33.7 mm
  f0: cylinder r=2.95mm len=33.74mm, axis (0,0,-1), area 625.3mm2, adj f1,f2
  f1: plane 5.9x5.9mm, normal (0,0,-1), area 27.3mm2, adj f0
  f2: plane 5.9x5.9mm, normal (0,0,1), area 27.3mm2, adj f0
PLACE A rot(axis=(0.44,0.44,0.78),104.1deg) t=(-45.36,-57.26,70.33)mm
PLACE B rot(axis=(0,-1,0),120.8deg) t=(-62.17,-57.26,133.29)mm
PLACE C rot(axis=(0,-1,0),120.8deg) t=(-57.25,9.27,136.23)mm
PLACE D rot(axis=(0.61,0.71,0.36),179.4deg) t=(-106.22,-33.59,122.89)mm
PLACE E rot(axis=(0,1,0),25.3deg) t=(-67.04,-57.26,146.03)mm fixed
PLACE F rot(axis=(0,-1,0),120.8deg) t=(-58.7,9.27,135.36)mm
MATE cylindrical F.f0 <-> D.f0  axis (0.86,0,0.51) through (-87.67,-57.26,118.07)mm
MATE fastened A.f1 <-> F.f0  axis (-0.86,0,-0.51) through (-77.48,-57.26,124.16)mm
MATE revolute E.f4 <-> B.f0  axis (0,1,0) through (-62.17,-50.31,133.29)mm
MATE fastened F.f0 <-> C.f0  axis (0.86,0,0.51) through (-87.67,-57.26,118.07)mm
MATE fastened F.f0 <-> B.f3  axis (0.86,0,0.51) through (-58.7,-57.26,135.36)mm
